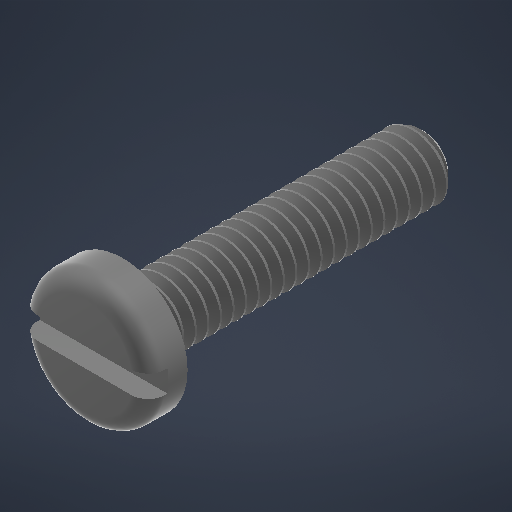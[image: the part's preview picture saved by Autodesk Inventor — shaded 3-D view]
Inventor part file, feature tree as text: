
AUTODESK INVENTOR PART (.ipt)
format: ipt  version: 2025.2 (Build 292293000, 293)  size: 548,864 bytes
history: native  units: in
note: dims shown in document units (in); Inventor stores cm internally (conversion verified against a paired STEP export)
features: other x1, extrude x1
ambient origin geometry x8: Origin, YZ Plane, XZ Plane, XY Plane, X Axis, Y Axis, Z Axis, Center Point
bodies: Solid1 (feature_tree)
feature tree (2):
  other  "Plane1"
  extrude  "Extrude15"  [1 undecoded]
note: 1 required parameter value undecoded (feature->parameter linkage not recoverable at this tier; creation-order binding heuristic only, values carry confidence <= 0.55)
